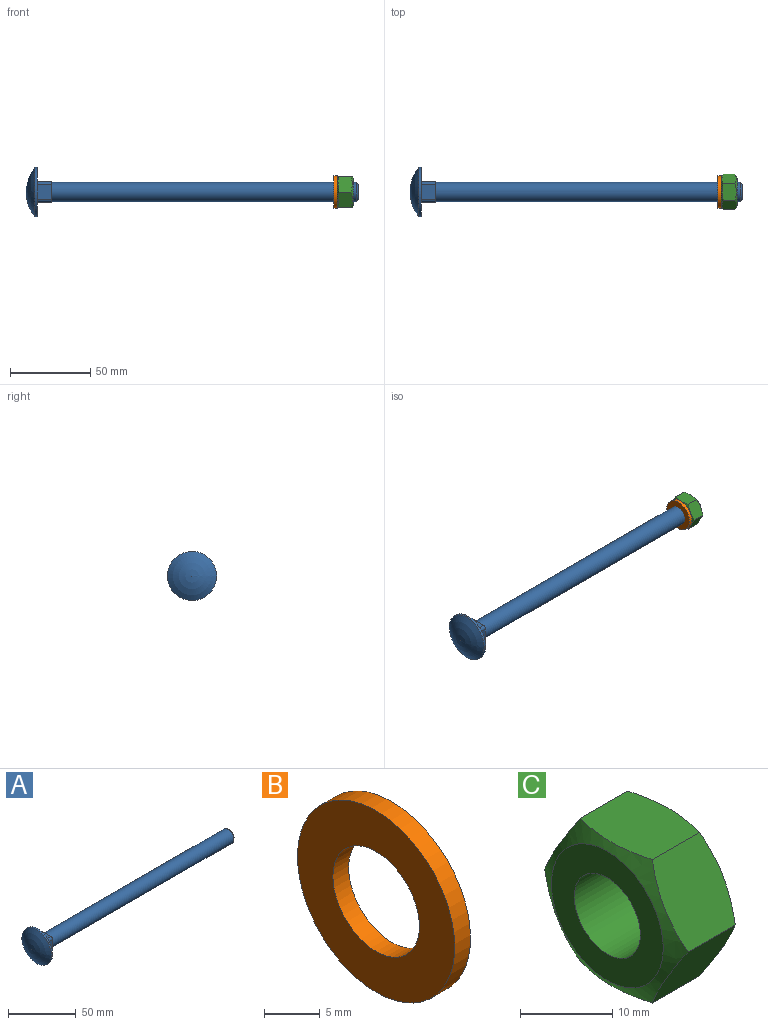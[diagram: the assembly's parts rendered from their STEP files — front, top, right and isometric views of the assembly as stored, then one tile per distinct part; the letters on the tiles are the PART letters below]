
ASSEMBLY  parts=3 mates=2
PART A: 15 faces, bbox 207x30.7x30.7 mm
  f0: plane 9.1x8.75mm, normal (0,1,0), area 79.6mm2, adj f4,f5,f10,f11
  f1: plane 9.1x8.75mm, normal (0,0,1), area 79.6mm2, adj f4,f5,f8,f11
  f2: plane 9.1x8.75mm, normal (0,-1,0), area 79.6mm2, adj f4,f5,f8,f9
  f3: plane 9.1x8.75mm, normal (0,0,-1), area 79.6mm2, adj f4,f5,f9,f10
  f4: plane 12.7x12.7mm, normal (1,0,0), area 45.4mm2, adj f0,f1,f2,f3,f8,f9,f10,f11
  f5: plane 30.65x30.65mm, normal (1,0,0), area 579.3mm2, adj f0,f1,f2,f3,f6,f8,f9,f10
  f6: cylinder r=15.32mm len=30.65mm, axis (-1,0,0), area 139.6mm2, adj f5,f7
  f7: sphere r=24.1mm, area 832.9mm2, adj f6
  f8: cylinder r=1.8mm len=8.75mm, axis (-1,0,0), area 24.7mm2, adj f1,f2,f4,f5
  f9: cylinder r=1.8mm len=8.75mm, axis (-1,0,0), area 24.7mm2, adj f2,f3,f4,f5
  f10: cylinder r=1.8mm len=8.75mm, axis (-1,0,0), area 24.7mm2, adj f0,f3,f4,f5
  f11: cylinder r=1.8mm len=8.75mm, axis (-1,0,0), area 24.7mm2, adj f0,f1,f4,f5
  f12: cylinder r=6mm len=190.18mm, axis (1,0,0), area 7169.5mm2, adj f4,f13
  f13: cone r=6mm half-angle=45deg, axis (-1,0,0), area 52.1mm2, adj f12,f14
  f14: plane 9.85x9.85mm, normal (1,0,0), area 76.2mm2, adj f13
PART B: 4 faces, bbox 2x20x20 mm
  f0: plane 20x20mm, normal (-1,0,0), area 219.1mm2, adj f1,f3
  f1: cylinder r=5.5mm len=11mm, axis (1,0,0), area 69.1mm2, adj f0,f2
  f2: plane 20x20mm, normal (1,0,0), area 219.1mm2, adj f1,f3
  f3: cylinder r=10mm len=20mm, axis (1,0,0), area 125.7mm2, adj f0,f2
PART C: 11 faces, bbox 10x21.9x21.9 mm
  f0: plane 17.1x17.1mm, normal (1,0,0), area 149.4mm2, adj f1,f4
  f1: cone r=11.4mm half-angle=60deg, axis (-1,0,0), area 95.8mm2, adj f0,f5,f6,f7,f8,f9,f10
  f2: cone r=8.55mm half-angle=60deg, axis (1,0,0), area 95.8mm2, adj f3,f5,f6,f7,f8,f9,f10
  f3: plane 17.1x17.1mm, normal (-1,0,0), area 149.4mm2, adj f2,f4
  f4: cylinder r=5.05mm len=10.11mm, axis (1,0,0), area 317.5mm2, adj f0,f3
  f5: plane 10.98x8.91mm, normal (0,0,1), area 91.3mm2, adj f1,f2,f6,f10
  f6: plane 9.5x8.91mm, normal (0,0.87,0.5), area 91.3mm2, adj f1,f2,f5,f7
  f7: plane 9.5x8.91mm, normal (0,0.87,-0.5), area 91.3mm2, adj f1,f2,f6,f8
  f8: plane 10.98x8.91mm, normal (0,0,-1), area 91.3mm2, adj f1,f2,f7,f9
  f9: plane 9.5x8.91mm, normal (0,-0.87,-0.5), area 91.3mm2, adj f1,f2,f8,f10
  f10: plane 9.5x8.91mm, normal (0,-0.87,0.5), area 91.3mm2, adj f1,f2,f5,f9
PLACE A at identity fixed
PLACE B t=(185,0,0)mm
PLACE C t=(187,0,0)mm
MATE fastened B.f1 <-> A.f12  axis (-1,0,0) through (185,0,0)mm
MATE fastened C.f1 <-> B.f1  axis (1,0,0) through (187,0,0)mm
